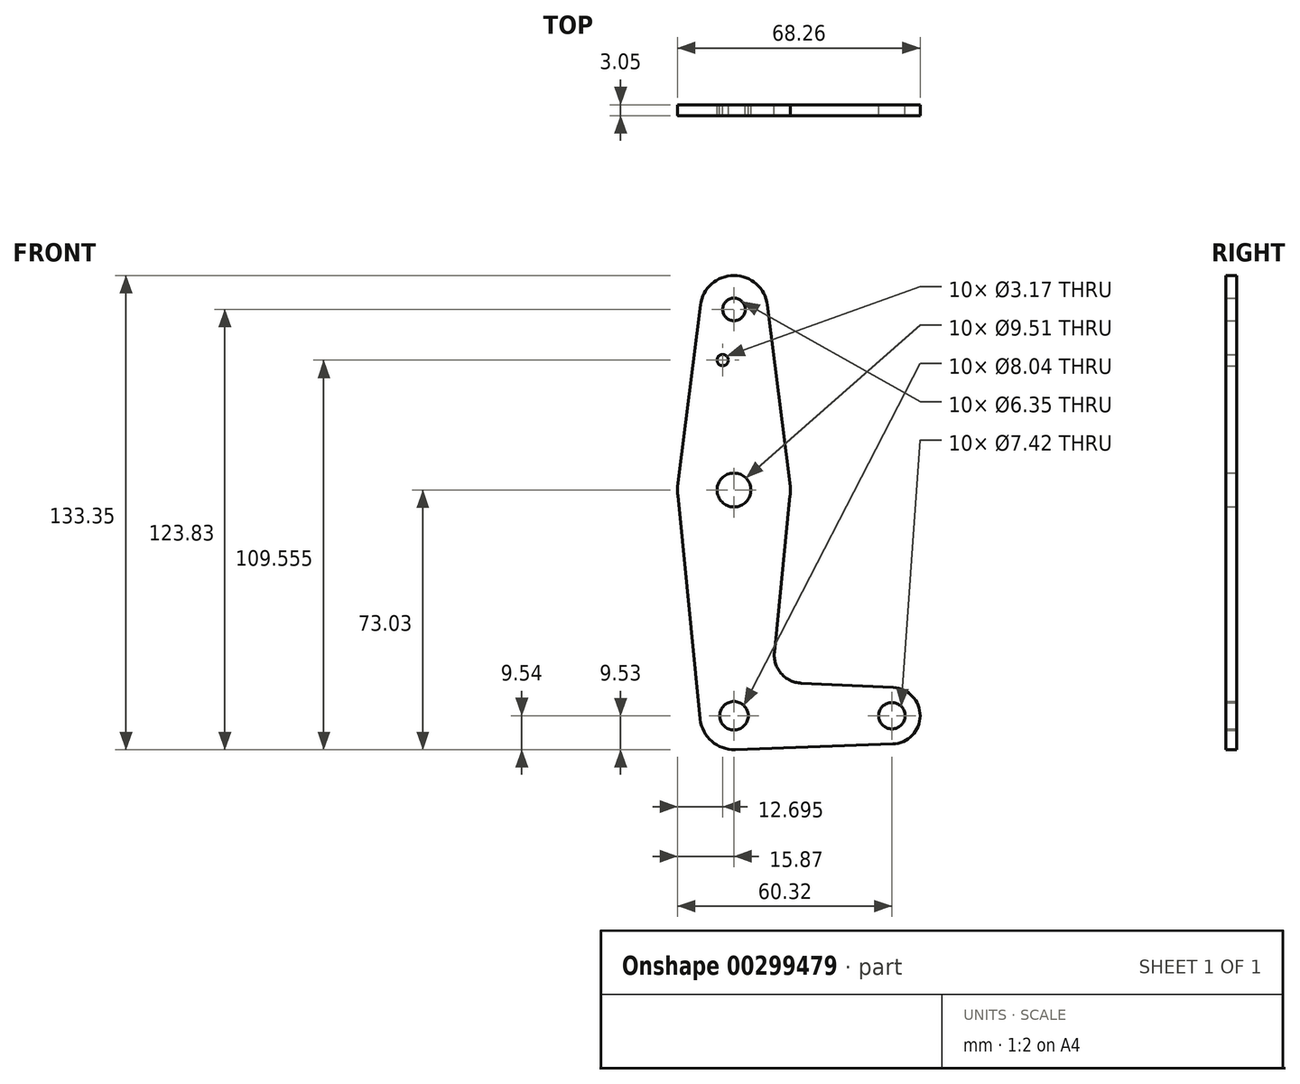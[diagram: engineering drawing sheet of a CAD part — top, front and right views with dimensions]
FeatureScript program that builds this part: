
annotation { "Feature Type Name" : "Feature", "Feature Type Description" : "" }
export const myFeature = defineFeature(function(context is Context, id is Id, definition is map)
    precondition{}
    {
        {
            var Q0;
            Q0=qCreatedBy(makeId("Front.planeOp"),FACE);
            var sketch = newSketch(context, id + "F0", { "sketchPlane" : qUnion([Q0])});
            skCircle(sketch, "E0", {"center": v(0, 0) * mm, "radius": 15.88 * mm});
            skCircle(sketch, "E1", {"center": v(44.45, -63.49) * mm, "radius": 7.94 * mm});
            skCircle(sketch, "E2", {"center": v(0, 50.8) * mm, "radius": 9.53 * mm});
            skLineSegment(sketch, "E3", {"start": v(0, 50.8) * mm, "end": v(0, 0) * mm, "construction": true});
            skLineSegment(sketch, "E4", {"start": v(0, 0) * mm, "end": v(0, -63.5) * mm, "construction": true});
            skLineSegment(sketch, "E5", {"start": v(0, -63.5) * mm, "end": v(44.45, -63.49) * mm, "construction": true});
            skLineSegment(sketch, "E6", {"start": v(-15.8, -1.59) * mm, "end": v(-9.48, -64.45) * mm});
            skLineSegment(sketch, "E7", {"start": v(45.07, -71.41) * mm, "end": v(45.21, -71.4) * mm});
            skLineSegment(sketch, "E8", {"start": v(45.21, -71.4) * mm, "end": v(45.07, -71.4) * mm});
            skPoint(sketch, "E9.endSnap0", {"position": v(45.14, -71.4) * mm});
            skLineSegment(sketch, "E10", {"start": v(0.34, -73.02) * mm, "end": v(45.14, -71.4) * mm});
            skLineSegment(sketch, "E11", {"start": v(-9.45, 52) * mm, "end": v(-15.75, 1.98) * mm});
            skLineSegment(sketch, "E12", {"start": v(9.45, 52) * mm, "end": v(15.75, 1.98) * mm});
            skCircle(sketch, "E13", {"center": v(-3.18, 36.53) * mm, "radius": 1.59 * mm});
            skCircle(sketch, "E14", {"center": v(0, 50.8) * mm, "radius": 3.18 * mm});
            skCircle(sketch, "E15", {"center": v(0, 0) * mm, "radius": 4.76 * mm});
            skCircle(sketch, "E16", {"center": v(0, -63.5) * mm, "radius": 4.02 * mm});
            skCircle(sketch, "E17", {"center": v(44.45, -63.49) * mm, "radius": 3.7 * mm});
            skCircle(sketch, "E18", {"center": v(0, -63.5) * mm, "radius": 9.53 * mm});
            skLineSegment(sketch, "E19", {"start": v(15.8, -1.59) * mm, "end": v(11.37, -45.59) * mm});
            skLineSegment(sketch, "E20", {"start": v(44.83, -55.56) * mm, "end": v(18.9, -54.33) * mm});
            skArc(sketch, "E21.filletArc", {"start": v(11.37, -45.59) * mm, "mid": v(13.26, -51.58) * mm, "end": v(18.9, -54.33) * mm});
            skSolve(sketch);
        }
        {
            var Q0;
            Q0 = qSketchRegion(id + "F0", true);
            extrude(context, id + "F1", {"entities" : qUnion([Q0]), "depth" : 3.05 * mm});
        }
    });
